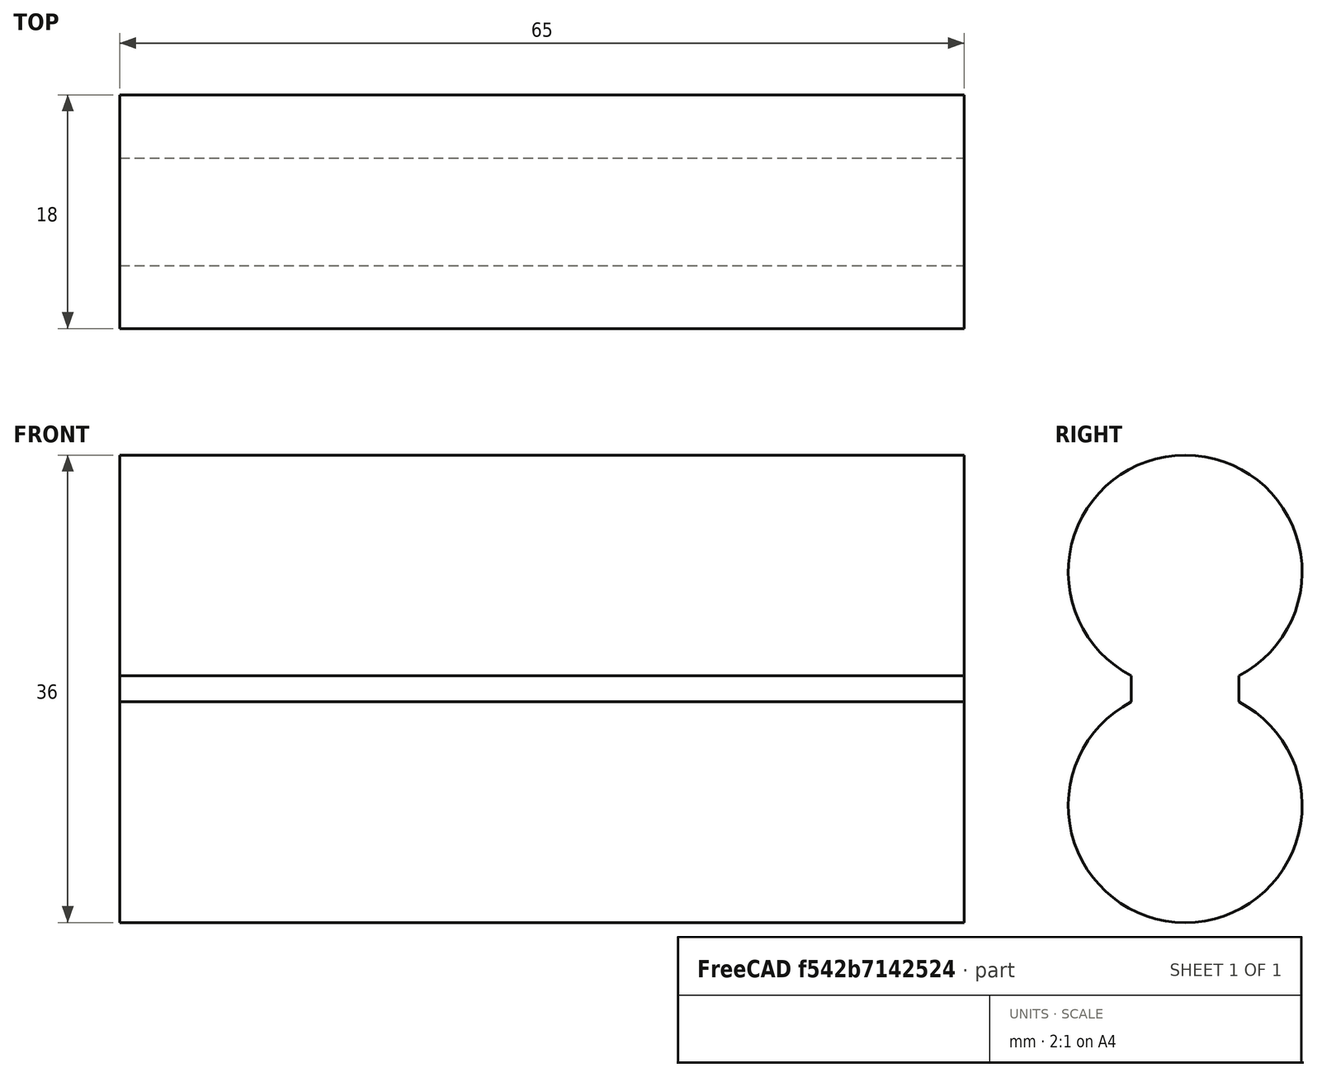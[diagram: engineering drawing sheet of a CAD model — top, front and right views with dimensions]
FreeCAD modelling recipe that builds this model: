
FCSTD DOCUMENT  (FreeCAD 0.18R16131 (Git))
Label: batt_2x_18650
License: All rights reserved
LicenseURL: http://en.wikipedia.org/wiki/All_rights_reserved
objects: Sketcher::SketchObject×1, PartDesign::Pad×1, PartDesign::Body×1
note: 4 computed .brp shape members not serialized (recipe doc carries the construction recipe); baked Part::Feature solids carry a one-line shape summary decoded from their .brp

FEATURE [Sketcher::SketchObject] Sketch
  MapMode = 5
  Placement = pos=(0,0,0) rot=(0.57735,0.57735,0.57735;2.0944rad)
  Support = -> [YZ_Plane]
  sketch-geometry (4):
    g0: ArcOfCircle CenterX=0 CenterY=-10 CenterZ=0 NormalX=0 NormalY=0 NormalZ=1 AngleXU=0 Radius=9 StartAngle=5.19053 EndAngle=10.5174
    g1: ArcOfCircle CenterX=0 CenterY=-28 CenterZ=0 NormalX=0 NormalY=0 NormalZ=1 AngleXU=0 Radius=9 StartAngle=2.04894 EndAngle=7.37584
    g2: LineSegment StartX=-4.14119 StartY=-20.0093 StartZ=0 EndX=-4.14119 EndY=-17.9907 EndZ=0
    g3: LineSegment StartX=4.14119 StartY=-17.9907 StartZ=0 EndX=4.14119 EndY=-20.0093 EndZ=0
  constraints (13):
    c: PointOnObject(g0,g-2)
    c: PointOnObject(g1,g-2)
    c: Coincident(g2,g1)
    c: Coincident(g2,g0)
    c: Coincident(g3,g0)
    c: Coincident(g3,g1)
    c: Vertical(g3)
    c: Vertical(g2)
    c: Equal(g3,g2)
    c: Equal(g0,g1)
    c: Radius(g0) = 9
    c: DistanceY(g1,g0) = 18
    c: DistanceY(g0,g-1) = 10
FEATURE [PartDesign::Pad] Pad
  Length = 65
  Length2 = 100
  Midplane = true
  Placement = pos=(0,0,0) rot=(0.57735,0.57735,0.57735;2.0944rad)
  Profile = -> Sketch
  Type = 0
FEATURE [PartDesign::Body] Body
  Group = -> [Sketch,Pad]
  Origin = -> Origin
  Tip = -> Pad
